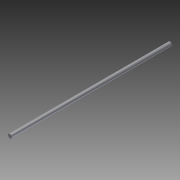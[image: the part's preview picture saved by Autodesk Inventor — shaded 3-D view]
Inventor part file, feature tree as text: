
AUTODESK INVENTOR PART (.ipt)
format: ipt  version: 2012 (Build 160160000, 160)  size: 62,464 bytes
history: native  units: in
note: dims shown in document units (in); Inventor stores cm internally (conversion verified against a paired STEP export)
features: extrude x1, sketch x1
ambient origin geometry x8: Origin, YZ Plane, XZ Plane, XY Plane, X Axis, Y Axis, Z Axis, Center Point
bodies: Solid1 (feature_tree)
feature tree (2):
  extrude  "Extrusion1"  Depth=20.25in TaperAngle=0.0deg
  sketch  "Sketch1"  dims[d0=0.5in d1=20.25in d2=0.0in]
